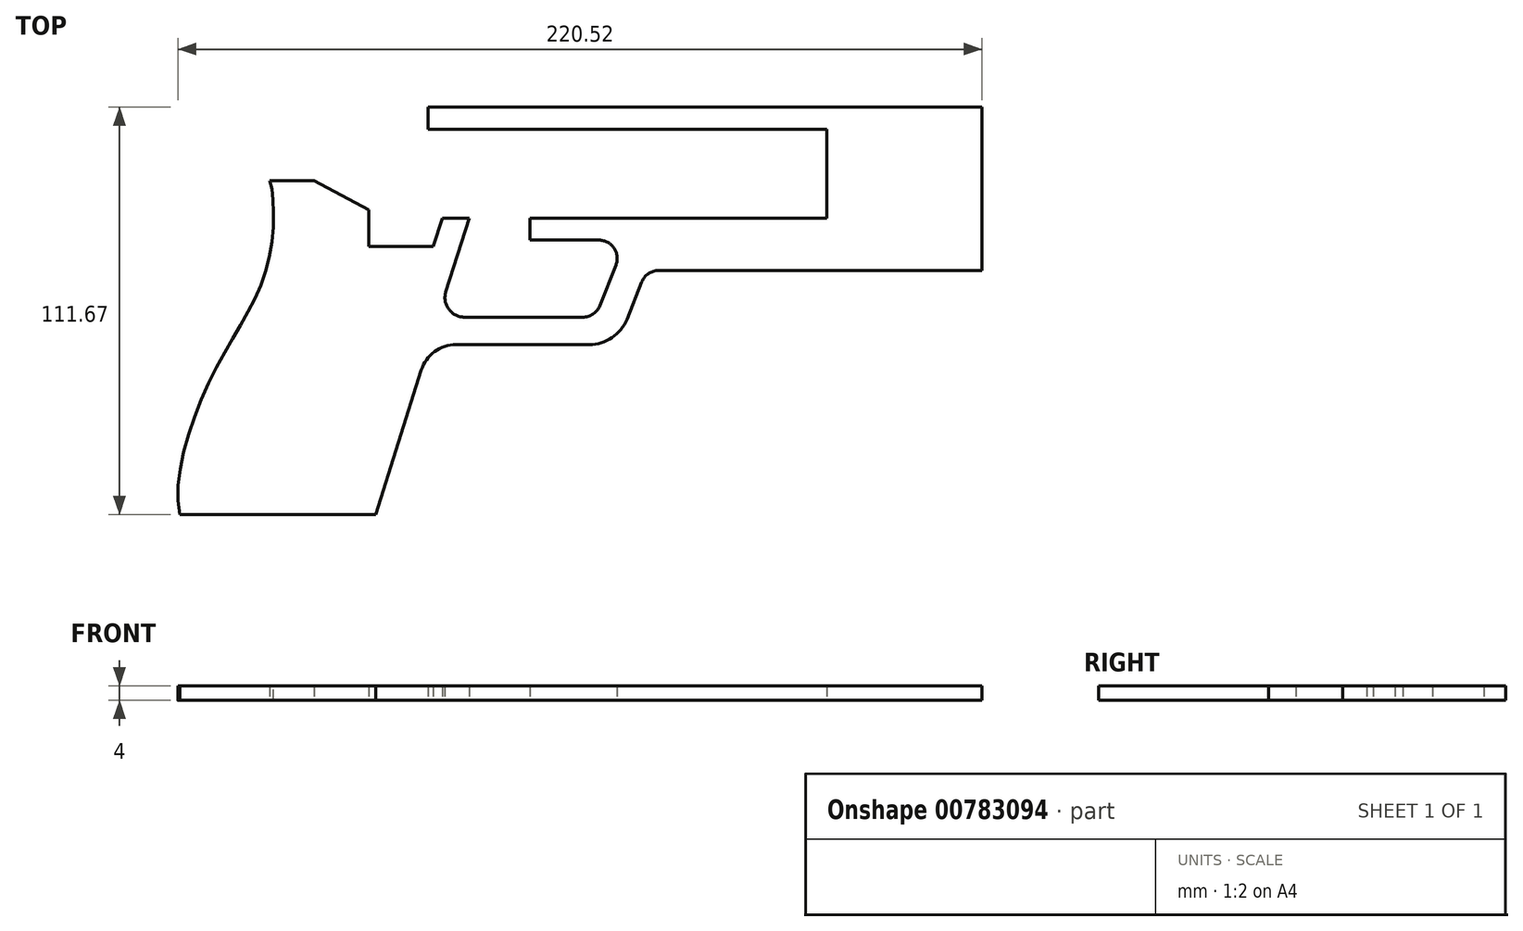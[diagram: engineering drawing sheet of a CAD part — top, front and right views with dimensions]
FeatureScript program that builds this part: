
annotation { "Feature Type Name" : "Feature", "Feature Type Description" : "" }
export const myFeature = defineFeature(function(context is Context, id is Id, definition is map)
    precondition{}
    {
        {
            var Q0;
            Q0=qCreatedBy(makeId("Top.planeOp"),FACE);
            var sketch = newSketch(context, id + "F0", { "sketchPlane" : qUnion([Q0])});
            skLineSegment(sketch, "E0", {"start": v(-129.35, 80.08) * mm, "end": v(90.65, 80.08) * mm});
            skLineSegment(sketch, "E1", {"start": v(-55.81, -2.87) * mm, "end": v(-19.3, -2.87) * mm});
            skLineSegment(sketch, "E2", {"start": v(-8.93, 4.18) * mm, "end": v(-4.89, 14.33) * mm});
            skLineSegment(sketch, "E3", {"start": v(-63.51, 62.25) * mm, "end": v(-63.51, 56.24) * mm});
            skLineSegment(sketch, "E4", {"start": v(-63.51, 56.24) * mm, "end": v(45.82, 56.24) * mm});
            skLineSegment(sketch, "E5", {"start": v(45.82, 56.24) * mm, "end": v(45.82, 31.9) * mm});
            skLineSegment(sketch, "E6", {"start": v(-106.86, 42.1) * mm, "end": v(-94.75, 42.1) * mm});
            skLineSegment(sketch, "E7", {"start": v(45.82, 31.9) * mm, "end": v(-35.48, 31.9) * mm});
            skLineSegment(sketch, "E8", {"start": v(-35.48, 25.89) * mm, "end": v(-35.48, 31.9) * mm});
            skLineSegment(sketch, "E9", {"start": v(-52.23, 31.9) * mm, "end": v(-59.6, 31.9) * mm});
            skLineSegment(sketch, "E10", {"start": v(-35.48, 25.89) * mm, "end": v(-16.6, 25.82) * mm});
            skLineSegment(sketch, "E11", {"start": v(-131.6, -49.42) * mm, "end": v(-77.83, -49.42) * mm});
            skFitSpline(sketch, "E12", {"points": [v(-131.6, -49.42) * mm, v(-122.39, -10.77) * mm, v(-107.52, 18.97) * mm, v(-106.86, 42.1) * mm], "startDerivative": vector(-17.74, 82.06) * mm, "endDerivative": vector(-13.54, 41.4) * mm});
            skLineSegment(sketch, "E13", {"start": v(-63.51, 62.25) * mm, "end": v(88.4, 62.25) * mm});
            skLineSegment(sketch, "E14", {"start": v(-77.83, -49.42) * mm, "end": v(-65.35, -9.86) * mm});
            skLineSegment(sketch, "E15", {"start": v(-52.23, 31.9) * mm, "end": v(-58.6, 11.68) * mm});
            skLineSegment(sketch, "E16", {"start": v(-59.6, 31.9) * mm, "end": v(-62.07, 24.08) * mm});
            skLineSegment(sketch, "E17", {"start": v(-62.07, 24.08) * mm, "end": v(-79.8, 24.08) * mm});
            skLineSegment(sketch, "E18", {"start": v(-79.8, 24.08) * mm, "end": v(-79.8, 34.08) * mm});
            skLineSegment(sketch, "E19", {"start": v(-79.8, 34.08) * mm, "end": v(-94.75, 42.1) * mm});
            skPoint(sketch, "E20.visualSharp", {"position": v(-11.73, -2.87) * mm});
            skArc(sketch, "E20.filletArc", {"start": v(-19.3, -2.87) * mm, "mid": v(-13.04, -0.94) * mm, "end": v(-8.93, 4.18) * mm});
            skPoint(sketch, "E21.visualSharp", {"position": v(-63.2, -2.87) * mm});
            skArc(sketch, "E21.filletArc", {"start": v(-55.81, -2.87) * mm, "mid": v(-61.72, -4.8) * mm, "end": v(-65.35, -9.86) * mm});
            skLineSegment(sketch, "E22", {"start": v(-11.98, 18.97) * mm, "end": v(-16.4, 7.84) * mm});
            skLineSegment(sketch, "E23", {"start": v(-21.05, 4.69) * mm, "end": v(-53.48, 4.69) * mm});
            skPoint(sketch, "E24.visualSharp", {"position": v(-60.81, 4.69) * mm});
            skArc(sketch, "E24.filletArc", {"start": v(-58.6, 11.68) * mm, "mid": v(-57.82, 6.89) * mm, "end": v(-53.48, 4.69) * mm});
            skPoint(sketch, "E25.visualSharp", {"position": v(-17.65, 4.69) * mm});
            skArc(sketch, "E25.filletArc", {"start": v(-21.05, 4.69) * mm, "mid": v(-18.24, 5.55) * mm, "end": v(-16.4, 7.84) * mm});
            skPoint(sketch, "E26.visualSharp", {"position": v(-9.27, 25.8) * mm});
            skArc(sketch, "E26.filletArc", {"start": v(-11.98, 18.97) * mm, "mid": v(-12.48, 23.62) * mm, "end": v(-16.6, 25.82) * mm});
            skPoint(sketch, "E27.visualSharp", {"position": v(-3.64, 17.49) * mm});
            skArc(sketch, "E27.filletArc", {"start": v(-0.24, 17.49) * mm, "mid": v(-3.05, 16.62) * mm, "end": v(-4.89, 14.33) * mm});
            skLineSegment(sketch, "E28", {"start": v(-0.24, 17.49) * mm, "end": v(88.4, 17.49) * mm});
            skLineSegment(sketch, "E29", {"start": v(88.4, 62.25) * mm, "end": v(88.4, 17.49) * mm});
            skSolve(sketch);
        }
        {
            var Q0;
            Q0 = qSketchRegion(id + "F0", true);
            extrude(context, id + "F1", {"entities" : qUnion([Q0]), "depth" : 4 * mm, "offsetDistance" : 25 * mm});
        }
    });
